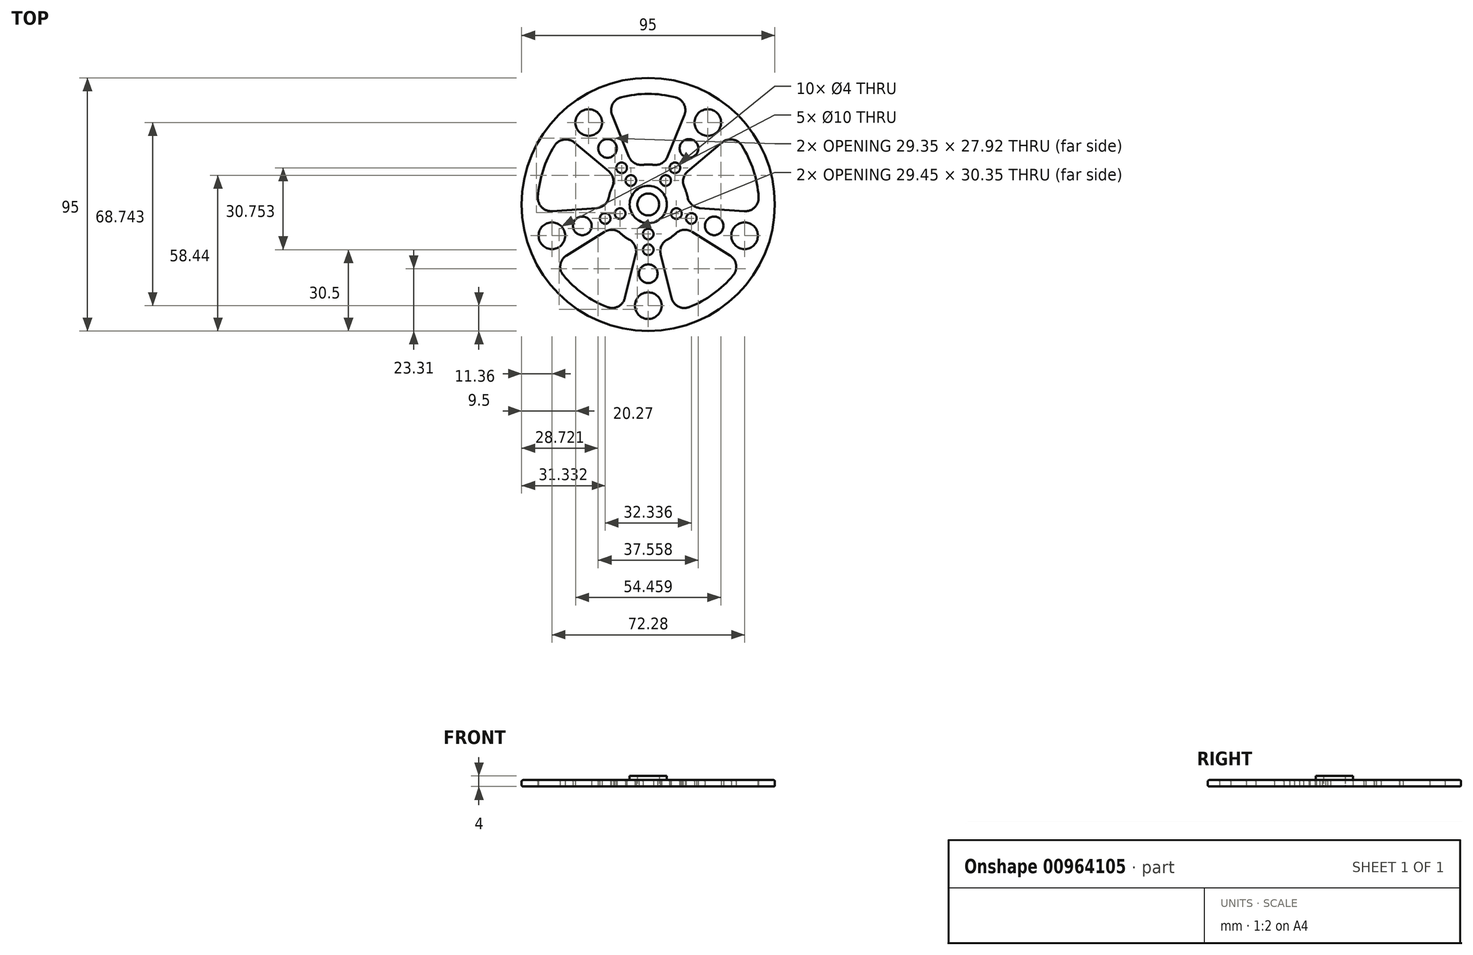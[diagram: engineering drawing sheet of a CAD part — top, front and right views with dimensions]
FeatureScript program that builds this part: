
annotation { "Feature Type Name" : "Feature", "Feature Type Description" : "" }
export const myFeature = defineFeature(function(context is Context, id is Id, definition is map)
    precondition{}
    {
        {
            var Q0;
            Q0=qCreatedBy(makeId("Top.planeOp"),FACE);
            var sketch = newSketch(context, id + "F0", { "sketchPlane" : qUnion([Q0])});
            skCircle(sketch, "E0", {"center": v(0, 0) * mm, "radius": 47.5 * mm});
            skCircle(sketch, "E1", {"center": v(0, 0) * mm, "radius": 15 * mm});
            skCircle(sketch, "E2", {"center": v(0, 0) * mm, "radius": 41.5 * mm});
            skLineSegment(sketch, "E3", {"start": v(0, 0) * mm, "end": v(0, 47.5) * mm});
            skLineSegment(sketch, "E4", {"start": v(0, 0) * mm, "end": v(27.92, 38.43) * mm});
            skLineSegment(sketch, "E5.MirrorCS", {"start": v(0, 0) * mm, "end": v(-27.92, 38.43) * mm});
            skLineSegment(sketch, "E6", {"start": v(0, 0) * mm, "end": v(17.8, 44.04) * mm});
            skLineSegment(sketch, "E7.MirrorCS", {"start": v(0, 0) * mm, "end": v(-17.8, 44.04) * mm});
            skCircle(sketch, "E8", {"center": v(-10, 13.75) * mm, "radius": 2 * mm});
            skCircle(sketch, "E9", {"center": v(-15.28, 21.03) * mm, "radius": 3.5 * mm});
            skCircle(sketch, "E10", {"center": v(-22.34, 30.74) * mm, "radius": 5 * mm});
            skCircle(sketch, "E11.MirrorC", {"center": v(22.34, 30.74) * mm, "radius": 5 * mm});
            skCircle(sketch, "E12.MirrorC", {"center": v(15.28, 21.03) * mm, "radius": 3.5 * mm});
            skCircle(sketch, "E13.MirrorC", {"center": v(10, 13.75) * mm, "radius": 2 * mm});
            skCircle(sketch, "E14", {"center": v(0, 0) * mm, "radius": 11.1 * mm});
            skCircle(sketch, "E15", {"center": v(0, 0) * mm, "radius": 4.1 * mm});
            skCircle(sketch, "E16", {"center": v(-6.52, 8.98) * mm, "radius": 2 * mm});
            skCircle(sketch, "E17.MirrorC", {"center": v(6.52, 8.98) * mm, "radius": 2 * mm});
            skCircle(sketch, "E18", {"center": v(0, 0) * mm, "radius": 7 * mm});
            skSolve(sketch);
        }
        {
            var Q0;
            {var subQ8=sQuery(id+"F0.wireOp",EDGE,"E7.MirrorCS");var subQ12=sQuery(id+"F0.wireOp",EDGE,"E1");var subQ13=makeQuery(id+"F0.imprint","INTERSECT",VERTEX,{"derivedFrom":[subQ12,subQ8]});Q0=makeQuery(id+"F0.imprint","IMPRINT",FACE,{"disambiguationData":[TD([[makeQuery(id+"F0.imprint","IMPRINT",EDGE,{"disambiguationData":[TD([[subQ13,-1.0]])],"derivedFrom":subQ12}),-1.0]])]});}
            var Q1;
            {var subQ0=sQuery(id+"F0.wireOp",EDGE,"E5.MirrorCS");var subQ1=sQuery(id+"F0.wireOp",EDGE,"E0");var subQ2=makeQuery(id+"F0.imprint","INTERSECT",VERTEX,{"derivedFrom":[subQ1,subQ0]});Q1=makeQuery(id+"F0.imprint","IMPRINT",FACE,{"disambiguationData":[TD([[makeQuery(id+"F0.imprint","IMPRINT",EDGE,{"disambiguationData":[TD([[subQ2,1.0]])],"derivedFrom":subQ1}),1.0]])]});}
            var Q2;
            {var subQ0=sQuery(id+"F0.wireOp",EDGE,"E3");var subQ1=sQuery(id+"F0.wireOp",EDGE,"E0");var subQ2=makeQuery(id+"F0.imprint","INTERSECT",VERTEX,{"derivedFrom":[subQ1,subQ0]});Q2=makeQuery(id+"F0.imprint","IMPRINT",FACE,{"disambiguationData":[TD([[makeQuery(id+"F0.imprint","IMPRINT",EDGE,{"disambiguationData":[TD([[subQ2,-1.0]])],"derivedFrom":subQ1}),1.0]])]});}
            var Q3;
            {var subQ0=sQuery(id+"F0.wireOp",EDGE,"E3");var subQ1=sQuery(id+"F0.wireOp",EDGE,"E0");var subQ2=makeQuery(id+"F0.imprint","INTERSECT",VERTEX,{"derivedFrom":[subQ1,subQ0]});Q3=makeQuery(id+"F0.imprint","IMPRINT",FACE,{"disambiguationData":[TD([[makeQuery(id+"F0.imprint","IMPRINT",EDGE,{"disambiguationData":[TD([[subQ2,1.0]])],"derivedFrom":subQ1}),1.0]])]});}
            var Q4;
            {var subQ0=sQuery(id+"F0.wireOp",EDGE,"E4");var subQ1=sQuery(id+"F0.wireOp",EDGE,"E0");var subQ2=makeQuery(id+"F0.imprint","INTERSECT",VERTEX,{"derivedFrom":[subQ1,subQ0]});Q4=makeQuery(id+"F0.imprint","IMPRINT",FACE,{"disambiguationData":[TD([[makeQuery(id+"F0.imprint","IMPRINT",EDGE,{"disambiguationData":[TD([[subQ2,-1.0]])],"derivedFrom":subQ1}),1.0]])]});}
            var Q5;
            {var subQ0=sQuery(id+"F0.wireOp",EDGE,"E13.MirrorC");var subQ9=sQuery(id+"F0.wireOp",EDGE,"E1");var subQ10=makeQuery(id+"F0.imprint","INTERSECT",VERTEX,{"disambiguationData":[OD(1.0)],"derivedFrom":[subQ9,subQ0]});Q5=makeQuery(id+"F0.imprint","IMPRINT",FACE,{"disambiguationData":[TD([[makeQuery(id+"F0.imprint","IMPRINT",EDGE,{"disambiguationData":[TD([[subQ10,-1.0]])],"derivedFrom":subQ9}),-1.0]])]});}
            var Q6;
            {var subQ0=sQuery(id+"F0.wireOp",EDGE,"E13.MirrorC");var subQ1=sQuery(id+"F0.wireOp",EDGE,"E1");var subQ2=makeQuery(id+"F0.imprint","INTERSECT",VERTEX,{"disambiguationData":[OD(1.0)],"derivedFrom":[subQ1,subQ0]});Q6=makeQuery(id+"F0.imprint","IMPRINT",FACE,{"disambiguationData":[TD([[makeQuery(id+"F0.imprint","IMPRINT",EDGE,{"disambiguationData":[TD([[subQ2,-1.0]])],"derivedFrom":subQ1}),1.0]])]});}
            var Q7;
            {var subQ0=sQuery(id+"F0.wireOp",EDGE,"E6");var subQ1=sQuery(id+"F0.wireOp",EDGE,"E1");var subQ2=makeQuery(id+"F0.imprint","INTERSECT",VERTEX,{"derivedFrom":[subQ1,subQ0]});Q7=makeQuery(id+"F0.imprint","IMPRINT",FACE,{"disambiguationData":[TD([[makeQuery(id+"F0.imprint","IMPRINT",EDGE,{"disambiguationData":[TD([[subQ2,-1.0]])],"derivedFrom":subQ1}),1.0]])]});}
            var Q8;
            {var subQ0=sQuery(id+"F0.wireOp",EDGE,"E3");var subQ1=sQuery(id+"F0.wireOp",EDGE,"E1");var subQ2=makeQuery(id+"F0.imprint","INTERSECT",VERTEX,{"derivedFrom":[subQ1,subQ0]});Q8=makeQuery(id+"F0.imprint","IMPRINT",FACE,{"disambiguationData":[TD([[makeQuery(id+"F0.imprint","IMPRINT",EDGE,{"disambiguationData":[TD([[subQ2,-1.0]])],"derivedFrom":subQ1}),1.0]])]});}
            var Q9;
            {var subQ0=sQuery(id+"F0.wireOp",EDGE,"E7.MirrorCS");var subQ1=sQuery(id+"F0.wireOp",EDGE,"E1");var subQ2=makeQuery(id+"F0.imprint","INTERSECT",VERTEX,{"derivedFrom":[subQ1,subQ0]});Q9=makeQuery(id+"F0.imprint","IMPRINT",FACE,{"disambiguationData":[TD([[makeQuery(id+"F0.imprint","IMPRINT",EDGE,{"disambiguationData":[TD([[subQ2,-1.0]])],"derivedFrom":subQ1}),1.0]])]});}
            var Q10;
            {var subQ5=sQuery(id+"F0.wireOp",EDGE,"E15");var subQ7=sQuery(id+"F0.wireOp",EDGE,"E5.MirrorCS");var subQ8=makeQuery(id+"F0.imprint","INTERSECT",VERTEX,{"derivedFrom":[subQ7,subQ5]});Q10=makeQuery(id+"F0.imprint","IMPRINT",FACE,{"disambiguationData":[TD([[makeQuery(id+"F0.imprint","IMPRINT",EDGE,{"disambiguationData":[TD([[subQ8,-1.0]])],"derivedFrom":subQ7}),-1.0]])]});}
            var Q11;
            {var subQ0=sQuery(id+"F0.wireOp",EDGE,"E15");var subQ1=sQuery(id+"F0.wireOp",EDGE,"E3");var subQ2=makeQuery(id+"F0.imprint","INTERSECT",VERTEX,{"derivedFrom":[subQ1,subQ0]});Q11=makeQuery(id+"F0.imprint","IMPRINT",FACE,{"disambiguationData":[TD([[makeQuery(id+"F0.imprint","IMPRINT",EDGE,{"disambiguationData":[TD([[subQ2,-1.0]])],"derivedFrom":subQ1}),1.0]])]});}
            var Q12;
            {var subQ0=sQuery(id+"F0.wireOp",EDGE,"E15");var subQ1=sQuery(id+"F0.wireOp",EDGE,"E3");var subQ2=makeQuery(id+"F0.imprint","INTERSECT",VERTEX,{"derivedFrom":[subQ1,subQ0]});Q12=makeQuery(id+"F0.imprint","IMPRINT",FACE,{"disambiguationData":[TD([[makeQuery(id+"F0.imprint","IMPRINT",EDGE,{"disambiguationData":[TD([[subQ2,-1.0]])],"derivedFrom":subQ1}),-1.0]])]});}
            var Q13;
            {var subQ5=sQuery(id+"F0.wireOp",EDGE,"E15");var subQ7=sQuery(id+"F0.wireOp",EDGE,"E4");var subQ8=makeQuery(id+"F0.imprint","INTERSECT",VERTEX,{"derivedFrom":[subQ7,subQ5]});Q13=makeQuery(id+"F0.imprint","IMPRINT",FACE,{"disambiguationData":[TD([[makeQuery(id+"F0.imprint","IMPRINT",EDGE,{"disambiguationData":[TD([[subQ8,-1.0]])],"derivedFrom":subQ7}),1.0]])]});}
            var Q14;
            {var subQ1=sQuery(id+"F0.wireOp",EDGE,"E5.MirrorCS");var subQ7=sQuery(id+"F0.wireOp",EDGE,"E18");var subQ9=makeQuery(id+"F0.imprint","INTERSECT",VERTEX,{"derivedFrom":[subQ1,subQ7]});Q14=makeQuery(id+"F0.imprint","IMPRINT",FACE,{"disambiguationData":[TD([[makeQuery(id+"F0.imprint","IMPRINT",EDGE,{"disambiguationData":[TD([[subQ9,-1.0]])],"derivedFrom":subQ1}),-1.0]])]});}
            var Q15;
            {var subQ0=sQuery(id+"F0.wireOp",EDGE,"E18");var subQ1=sQuery(id+"F0.wireOp",EDGE,"E3");var subQ2=makeQuery(id+"F0.imprint","INTERSECT",VERTEX,{"derivedFrom":[subQ1,subQ0]});Q15=makeQuery(id+"F0.imprint","IMPRINT",FACE,{"disambiguationData":[TD([[makeQuery(id+"F0.imprint","IMPRINT",EDGE,{"disambiguationData":[TD([[subQ2,-1.0]])],"derivedFrom":subQ1}),1.0]])]});}
            var Q16;
            {var subQ0=sQuery(id+"F0.wireOp",EDGE,"E18");var subQ1=sQuery(id+"F0.wireOp",EDGE,"E3");var subQ2=makeQuery(id+"F0.imprint","INTERSECT",VERTEX,{"derivedFrom":[subQ1,subQ0]});Q16=makeQuery(id+"F0.imprint","IMPRINT",FACE,{"disambiguationData":[TD([[makeQuery(id+"F0.imprint","IMPRINT",EDGE,{"disambiguationData":[TD([[subQ2,-1.0]])],"derivedFrom":subQ1}),-1.0]])]});}
            var Q17;
            {var subQ5=sQuery(id+"F0.wireOp",EDGE,"E18");var subQ7=sQuery(id+"F0.wireOp",EDGE,"E4");var subQ9=makeQuery(id+"F0.imprint","INTERSECT",VERTEX,{"derivedFrom":[subQ7,subQ5]});Q17=makeQuery(id+"F0.imprint","IMPRINT",FACE,{"disambiguationData":[TD([[makeQuery(id+"F0.imprint","IMPRINT",EDGE,{"disambiguationData":[TD([[subQ9,-1.0]])],"derivedFrom":subQ7}),1.0]])]});}
            extrude(context, id + "F1", {"entities" : qUnion([Q0, Q1, Q2, Q3, Q4, Q5, Q6, Q7, Q8, Q9, Q10, Q11, Q12, Q13, Q14, Q15, Q16, Q17]), "depth" : 2.4 * mm, "offsetDistance" : 25 * mm});
        }
        {
            var Q0;
            {var subQ0=sQuery(id+"F0.wireOp",EDGE,"E15");var subQ1=sQuery(id+"F0.wireOp",EDGE,"E5.MirrorCS");var subQ2=makeQuery(id+"F0.imprint","INTERSECT",VERTEX,{"derivedFrom":[subQ1,subQ0]});Q0=makeQuery(id+"F0.imprint","IMPRINT",FACE,{"disambiguationData":[TD([[makeQuery(id+"F0.imprint","IMPRINT",EDGE,{"disambiguationData":[TD([[subQ2,-1.0]])],"derivedFrom":subQ1}),-1.0]])]});}
            var Q1;
            {var subQ0=sQuery(id+"F0.wireOp",EDGE,"E15");var subQ1=sQuery(id+"F0.wireOp",EDGE,"E3");var subQ2=makeQuery(id+"F0.imprint","INTERSECT",VERTEX,{"derivedFrom":[subQ1,subQ0]});Q1=makeQuery(id+"F0.imprint","IMPRINT",FACE,{"disambiguationData":[TD([[makeQuery(id+"F0.imprint","IMPRINT",EDGE,{"disambiguationData":[TD([[subQ2,-1.0]])],"derivedFrom":subQ1}),1.0]])]});}
            var Q2;
            {var subQ0=sQuery(id+"F0.wireOp",EDGE,"E15");var subQ1=sQuery(id+"F0.wireOp",EDGE,"E3");var subQ2=makeQuery(id+"F0.imprint","INTERSECT",VERTEX,{"derivedFrom":[subQ1,subQ0]});Q2=makeQuery(id+"F0.imprint","IMPRINT",FACE,{"disambiguationData":[TD([[makeQuery(id+"F0.imprint","IMPRINT",EDGE,{"disambiguationData":[TD([[subQ2,-1.0]])],"derivedFrom":subQ1}),-1.0]])]});}
            var Q3;
            {var subQ0=sQuery(id+"F0.wireOp",EDGE,"E15");var subQ1=sQuery(id+"F0.wireOp",EDGE,"E4");var subQ2=makeQuery(id+"F0.imprint","INTERSECT",VERTEX,{"derivedFrom":[subQ1,subQ0]});Q3=makeQuery(id+"F0.imprint","IMPRINT",FACE,{"disambiguationData":[TD([[makeQuery(id+"F0.imprint","IMPRINT",EDGE,{"disambiguationData":[TD([[subQ2,-1.0]])],"derivedFrom":subQ1}),1.0]])]});}
            extrude(context, id + "F2", {"entities" : qUnion([Q0, Q1, Q2, Q3]), "operationType" : NewBodyOperationType.ADD, "depth" : 4 * mm, "offsetDistance" : 25 * mm});
        }
        {
            var Q0;
            Q0=qCreatedBy(makeId("Right.planeOp"),FACE);
            var sketch = newSketch(context, id + "F3", { "sketchPlane" : qUnion([Q0])});
            skLineSegment(sketch, "E19", {"start": v(0, 0) * mm, "end": v(0, 41.7) * mm, "construction": true});
            skSolve(sketch);
        }
        {
            var Q0;
            Q0=makeQuery(id+"F1.opExtrude","SWEPT_EDGE",EDGE,{"disambiguationData":[OSD([sQuery(id+"F0.wireOp",EDGE,"E2"),sQuery(id+"F0.wireOp",EDGE,"Uvu9NsHt-r8MN-Bku2-RMAG-uFay6ZMQz7yp")])]});
            var Q1;
            Q1=makeQuery(id+"F1.opExtrude","SWEPT_EDGE",EDGE,{"disambiguationData":[OSD([sQuery(id+"F0.wireOp",EDGE,"E2"),sQuery(id+"F0.wireOp",EDGE,"ZDBHfwXg-ozDK-Ar2F-n0KV-WGB0As6Zonv4")])]});
            var Q2;
            Q2=makeQuery(id+"F1.opExtrude","SWEPT_EDGE",EDGE,{"disambiguationData":[OSD([sQuery(id+"F0.wireOp",EDGE,"E1"),sQuery(id+"F0.wireOp",EDGE,"ZDBHfwXg-ozDK-Ar2F-n0KV-WGB0As6Zonv4")])]});
            var Q3;
            Q3=makeQuery(id+"F1.opExtrude","SWEPT_EDGE",EDGE,{"disambiguationData":[OSD([sQuery(id+"F0.wireOp",EDGE,"E1"),sQuery(id+"F0.wireOp",EDGE,"Uvu9NsHt-r8MN-Bku2-RMAG-uFay6ZMQz7yp")])]});
            fillet(context, id + "F4", {"entities" : qUnion([Q0, Q1, Q2, Q3]), "radius" : 5 * mm, "tangentPropagation" : true, "allowEdgeOverflow" : false});
        }
        {
            var Q0;
            Q0=makeQuery(id+"F1.opExtrude","SWEPT_BODY",BODY,{"disambiguationData":[OSD([sQuery(id+"F0.wireOp",EDGE,"E0"),sQuery(id+"F0.wireOp",EDGE,"E1"),sQuery(id+"F0.wireOp",EDGE,"E2"),sQuery(id+"F0.wireOp",EDGE,"E3"),sQuery(id+"F0.wireOp",EDGE,"S5mO9Nff-Qldc-vmzZ-qQ7R-mNiVZuzqjkac"),sQuery(id+"F0.wireOp",EDGE,"Uvu9NsHt-r8MN-Bku2-RMAG-uFay6ZMQz7yp"),sQuery(id+"F0.wireOp",EDGE,"ZDBHfwXg-ozDK-Ar2F-n0KV-WGB0As6Zonv4")])]});
            var Q1;
            Q1=sQuery(id+"F3.wireOp",EDGE,"E19");
            circularPattern(context, id + "F5", {"operationType" : NewBodyOperationType.ADD, "entities" : qUnion([Q0]), "axis" : qUnion([Q1]), "angle" : 360 * degree, "instanceCount" : 5, "equalSpace" : true});
        }
        {
            var Q0;
            {var subQ0=makeQuery(id+"F1.opExtrude","CAP_FACE",FACE,{"disambiguationData":[OSD([sQuery(id+"F0.wireOp",EDGE,"E0"),sQuery(id+"F0.wireOp",EDGE,"E1"),sQuery(id+"F0.wireOp",EDGE,"E2"),sQuery(id+"F0.wireOp",EDGE,"E4"),sQuery(id+"F0.wireOp",EDGE,"E5.MirrorCS"),sQuery(id+"F0.wireOp",EDGE,"E6"),sQuery(id+"F0.wireOp",EDGE,"E7.MirrorCS"),sQuery(id+"F0.wireOp",EDGE,"E8"),sQuery(id+"F0.wireOp",EDGE,"E9"),sQuery(id+"F0.wireOp",EDGE,"E10"),sQuery(id+"F0.wireOp",EDGE,"E11.MirrorC"),sQuery(id+"F0.wireOp",EDGE,"E12.MirrorC"),sQuery(id+"F0.wireOp",EDGE,"E13.MirrorC")])],"isStart":false});Q0=makeQuery(id+"F5.boolean.opBoolean","MERGE",FACE,{"derivedFrom":[subQ0,makeQuery(id+"F5.opPattern","COPY",FACE,{"derivedFrom":subQ0,"instanceName":"1"}),makeQuery(id+"F5.opPattern","COPY",FACE,{"derivedFrom":subQ0,"instanceName":"2"}),makeQuery(id+"F5.opPattern","COPY",FACE,{"derivedFrom":subQ0,"instanceName":"3"}),makeQuery(id+"F5.opPattern","COPY",FACE,{"derivedFrom":subQ0,"instanceName":"4"})]});}
            var Q1;
            {var subQ0=sQuery(id+"F0.wireOp",EDGE,"E14");var subQ1=makeQuery(id+"F1.opExtrude","CAP_FACE",FACE,{"disambiguationData":[OSD([sQuery(id+"F0.wireOp",EDGE,"E0"),sQuery(id+"F0.wireOp",EDGE,"E1"),sQuery(id+"F0.wireOp",EDGE,"E2"),sQuery(id+"F0.wireOp",EDGE,"E4"),sQuery(id+"F0.wireOp",EDGE,"E5.MirrorCS"),sQuery(id+"F0.wireOp",EDGE,"E6"),sQuery(id+"F0.wireOp",EDGE,"E7.MirrorCS"),sQuery(id+"F0.wireOp",EDGE,"E8"),sQuery(id+"F0.wireOp",EDGE,"E9"),sQuery(id+"F0.wireOp",EDGE,"E10"),sQuery(id+"F0.wireOp",EDGE,"E11.MirrorC"),sQuery(id+"F0.wireOp",EDGE,"E12.MirrorC"),sQuery(id+"F0.wireOp",EDGE,"E13.MirrorC"),subQ0])],"isStart":true});Q1=makeQuery(id+"FtqBXPr9l4gzQap_1.boolean.opBoolean","MERGE",FACE,{"derivedFrom":[makeQuery(id+"F5.boolean.opBoolean","MERGE",FACE,{"derivedFrom":[subQ1,makeQuery(id+"F5.opPattern","COPY",FACE,{"derivedFrom":subQ1,"instanceName":"1"}),makeQuery(id+"F5.opPattern","COPY",FACE,{"derivedFrom":subQ1,"instanceName":"2"}),makeQuery(id+"F5.opPattern","COPY",FACE,{"derivedFrom":subQ1,"instanceName":"3"}),makeQuery(id+"F5.opPattern","COPY",FACE,{"derivedFrom":subQ1,"instanceName":"4"})]}),makeQuery(id+"FtqBXPr9l4gzQap_1.opExtrude","CAP_FACE",FACE,{"disambiguationData":[OSD([subQ0,sQuery(id+"F0.wireOp",EDGE,"E15")])],"isStart":true})]});}
            fillet(context, id + "F6", {"entities" : qUnion([Q0, Q1]), "radius" : 0.5 * mm, "tangentPropagation" : true, "allowEdgeOverflow" : false});
        }
    });
